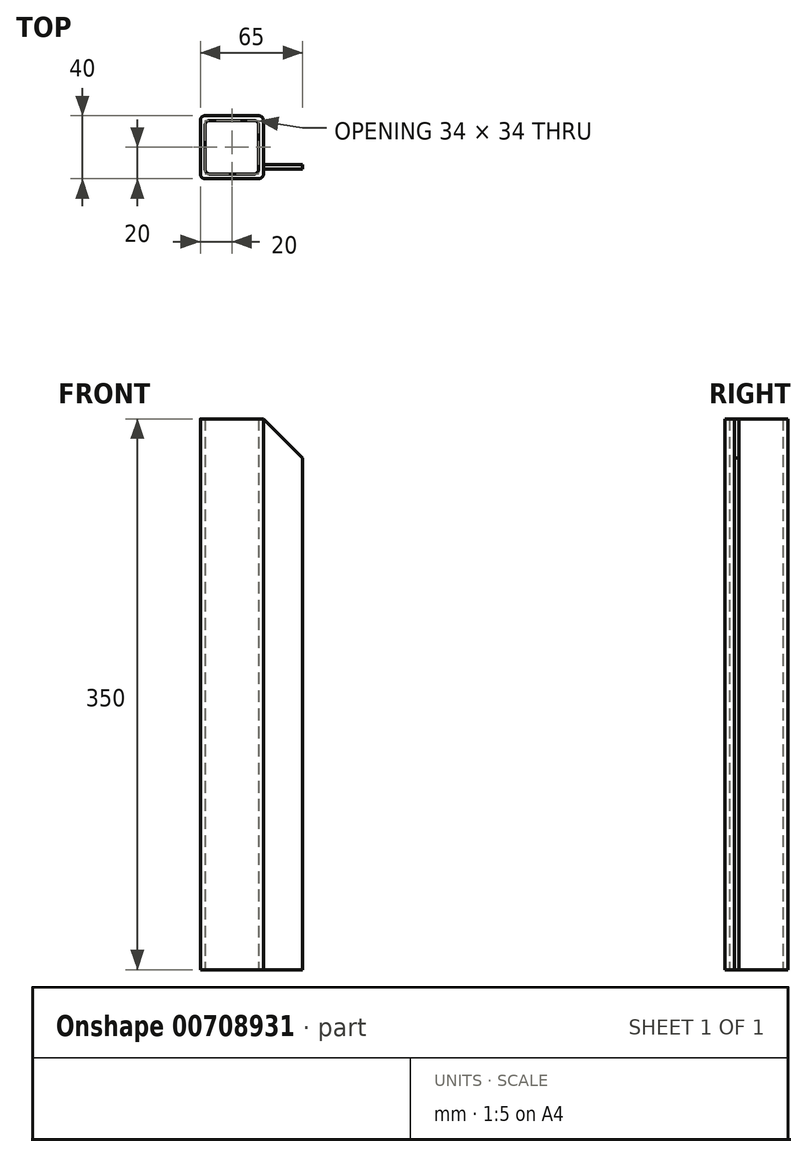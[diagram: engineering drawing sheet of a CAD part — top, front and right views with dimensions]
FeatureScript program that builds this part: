
annotation { "Feature Type Name" : "Feature", "Feature Type Description" : "" }
export const myFeature = defineFeature(function(context is Context, id is Id, definition is map)
    precondition{}
    {
        {
            var Q0;
            Q0=qCreatedBy(makeId("Top.planeOp"),FACE);
            var sketch = newSketch(context, id + "F0", { "sketchPlane" : qUnion([Q0])});
            skLineSegment(sketch, "E0.bottom", {"start": v(17, 20) * mm, "end": v(-17, 20) * mm});
            skLineSegment(sketch, "E0.top", {"start": v(17, -20) * mm, "end": v(-17, -20) * mm});
            skLineSegment(sketch, "E0.left", {"start": v(20, 17) * mm, "end": v(20, -17) * mm});
            skLineSegment(sketch, "E0.right", {"start": v(-20, 17) * mm, "end": v(-20, -17) * mm});
            skPoint(sketch, "E0.middle", {"position": v(0, 0) * mm});
            skLineSegment(sketch, "E1.0", {"start": v(17, 14) * mm, "end": v(17, -14) * mm});
            skLineSegment(sketch, "E1.1", {"start": v(14, 17) * mm, "end": v(-14, 17) * mm});
            skLineSegment(sketch, "E1.2", {"start": v(-17, 14) * mm, "end": v(-17, -14) * mm});
            skLineSegment(sketch, "E1.3", {"start": v(14, -17) * mm, "end": v(-14, -17) * mm});
            skPoint(sketch, "E2.visualSharp", {"position": v(17, 17) * mm});
            skArc(sketch, "E2.filletArc", {"start": v(17, 14) * mm, "mid": v(16.12, 16.12) * mm, "end": v(14, 17) * mm});
            skPoint(sketch, "E3.visualSharp", {"position": v(20, 20) * mm});
            skArc(sketch, "E3.filletArc", {"start": v(20, 17) * mm, "mid": v(19.12, 19.12) * mm, "end": v(17, 20) * mm});
            skPoint(sketch, "E4.visualSharp", {"position": v(17, -17) * mm});
            skArc(sketch, "E4.filletArc", {"start": v(14, -17) * mm, "mid": v(16.12, -16.12) * mm, "end": v(17, -14) * mm});
            skPoint(sketch, "E5.visualSharp", {"position": v(20, -20) * mm});
            skArc(sketch, "E5.filletArc", {"start": v(17, -20) * mm, "mid": v(19.12, -19.12) * mm, "end": v(20, -17) * mm});
            skPoint(sketch, "E6.visualSharp", {"position": v(-17, -17) * mm});
            skArc(sketch, "E6.filletArc", {"start": v(-17, -14) * mm, "mid": v(-16.12, -16.12) * mm, "end": v(-14, -17) * mm});
            skPoint(sketch, "E7.visualSharp", {"position": v(-20, -20) * mm});
            skArc(sketch, "E7.filletArc", {"start": v(-20, -17) * mm, "mid": v(-19.12, -19.12) * mm, "end": v(-17, -20) * mm});
            skPoint(sketch, "E8.visualSharp", {"position": v(-17, 17) * mm});
            skArc(sketch, "E8.filletArc", {"start": v(-14, 17) * mm, "mid": v(-16.12, 16.12) * mm, "end": v(-17, 14) * mm});
            skPoint(sketch, "E9.visualSharp", {"position": v(-20, 20) * mm});
            skArc(sketch, "E9.filletArc", {"start": v(-17, 20) * mm, "mid": v(-19.12, 19.12) * mm, "end": v(-20, 17) * mm});
            skSolve(sketch);
        }
        {
            var Q0;
            Q0=qSketchRegion(id+"F0",true);
            extrude(context, id + "F1", {"entities" : qUnion([Q0]), "endBound" : BoundingType.SYMMETRIC, "depth" : 350 * mm, "offsetDistance" : 25 * mm});
        }
        {
            var Q0;
            Q0=makeQuery(id+"F1.opExtrude","SWEPT_FACE",FACE,{"disambiguationData":[OSD([sQuery(id+"F0.wireOp",EDGE,"E0.left")])]});
            var sketch = newSketch(context, id + "F2", { "sketchPlane" : qUnion([Q0])});
            skLineSegment(sketch, "E10", {"start": v(0, 175) * mm, "end": v(0, -175) * mm});
            skLineSegment(sketch, "E11.bottom", {"start": v(-14, 175) * mm, "end": v(-11, 175) * mm});
            skLineSegment(sketch, "E11.top", {"start": v(-14, -175) * mm, "end": v(-11, -175) * mm});
            skLineSegment(sketch, "E11.left", {"start": v(-14, 175) * mm, "end": v(-14, -175) * mm});
            skLineSegment(sketch, "E11.right", {"start": v(-11, 175) * mm, "end": v(-11, -175) * mm});
            skSolve(sketch);
        }
        {
            var Q0;
            Q0=qSketchRegion(id+"F2",true);
            extrude(context, id + "F3", {"entities" : qUnion([Q0]), "operationType" : NewBodyOperationType.ADD, "depth" : 25 * mm, "offsetDistance" : 25 * mm});
        }
        {
            var Q0;
            Q0=makeQuery(id+"F3.opExtrude","SWEPT_FACE",FACE,{"disambiguationData":[OSD([sQuery(id+"F2.wireOp",EDGE,"E11.left")])]});
            var sketch = newSketch(context, id + "F4", { "sketchPlane" : qUnion([Q0])});
            skLineSegment(sketch, "E12", {"start": v(20, 175) * mm, "end": v(45, 150) * mm});
            skLineSegment(sketch, "E13", {"start": v(45, 150) * mm, "end": v(45, 175) * mm});
            skLineSegment(sketch, "E14", {"start": v(45, 175) * mm, "end": v(20, 175) * mm});
            skSolve(sketch);
        }
        {
            var Q0;
            Q0=qSketchRegion(id+"F4",true);
            extrude(context, id + "F5", {"entities" : qUnion([Q0]), "operationType" : NewBodyOperationType.REMOVE, "endBound" : BoundingType.THROUGH_ALL, "oppositeDirection" : true, "depth" : 25 * mm, "offsetDistance" : 25 * mm});
        }
    });
